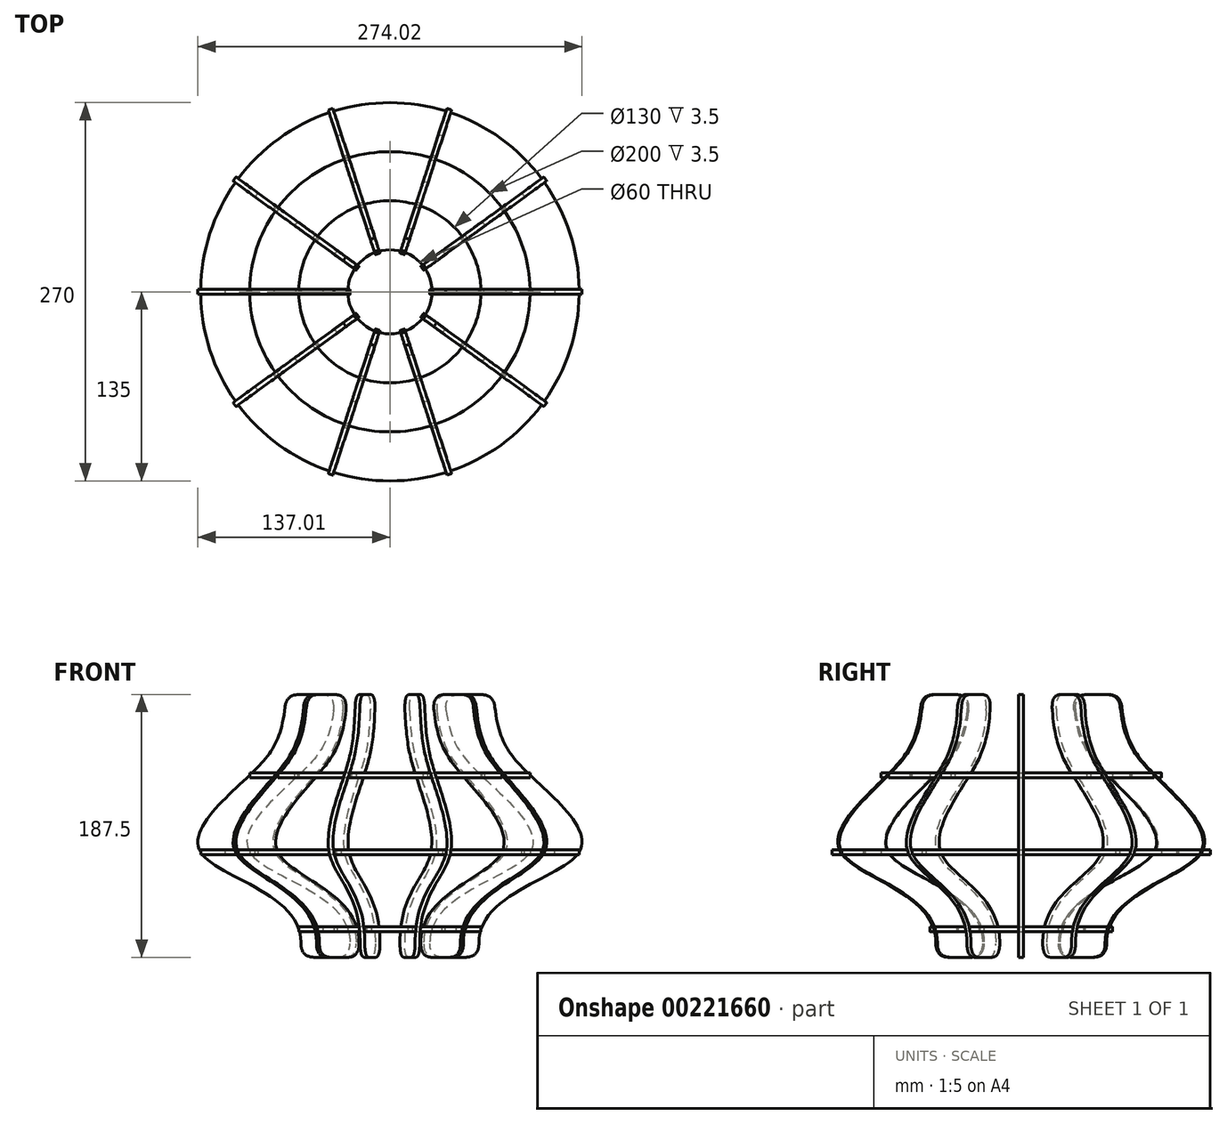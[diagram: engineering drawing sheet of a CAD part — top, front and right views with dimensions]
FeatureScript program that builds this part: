
annotation { "Feature Type Name" : "Feature", "Feature Type Description" : "" }
export const myFeature = defineFeature(function(context is Context, id is Id, definition is map)
    precondition{}
    {
        {
            assignVariable(context, id + "F0", {"name" : "m_thick", "anyValue" : 3.5 * mm});
        }
        {
            var Q0;
            Q0=qCreatedBy(makeId("Front.planeOp"),FACE);
            var sketch = newSketch(context, id + "F1", { "sketchPlane" : qUnion([Q0])});
            skFitSpline(sketch, "E0", {"points": [v(-74.04, 187.5) * mm, v(-100, 130) * mm, v(-135, 75) * mm, v(-65, 0) * mm], "startDerivative": vector(-20.16, -307.27) * mm, "endDerivative": vector(-98.43, -348.48) * mm});
            skLineSegment(sketch, "E1", {"start": v(-74.04, 187.5) * mm, "end": v(-39.04, 187.5) * mm});
            skLineSegment(sketch, "E2", {"start": v(-100, 130) * mm, "end": v(-65, 130) * mm, "construction": true});
            skLineSegment(sketch, "E3", {"start": v(-135, 75) * mm, "end": v(-100, 75) * mm, "construction": true});
            skLineSegment(sketch, "E4", {"start": v(-65, 0) * mm, "end": v(-30, 0) * mm});
            skLineSegment(sketch, "E5", {"start": v(-76.08, 156.38) * mm, "end": v(-41.08, 156.38) * mm, "construction": true});
            skLineSegment(sketch, "E6", {"start": v(-52.3, 45) * mm, "end": v(-17.3, 45) * mm, "construction": true});
            skFitSpline(sketch, "E7", {"points": [v(-39.04, 187.5) * mm, v(-65, 130) * mm, v(-100, 75) * mm, v(-30, 0) * mm], "startDerivative": vector(-20.16, -307.27) * mm, "endDerivative": vector(-98.43, -348.48) * mm});
            skLineSegment(sketch, "E8", {"start": v(-65, 0) * mm, "end": v(-65, 130) * mm, "construction": true});
            skLineSegment(sketch, "E9", {"start": v(-100, 130) * mm, "end": v(-100, 75) * mm, "construction": true});
            skLineSegment(sketch, "E10.bottom", {"start": v(-63.18, 131.75) * mm, "end": v(-100, 131.75) * mm});
            skLineSegment(sketch, "E10.top", {"start": v(-65, 128.25) * mm, "end": v(-100, 128.25) * mm});
            skLineSegment(sketch, "E10.left", {"start": v(-65, 131.75) * mm, "end": v(-65, 128.25) * mm});
            skLineSegment(sketch, "E10.right", {"start": v(-100, 131.75) * mm, "end": v(-100, 128.25) * mm});
            skPoint(sketch, "E10.middle", {"position": v(-82.5, 130) * mm});
            skLineSegment(sketch, "E11", {"start": v(-82.5, 128.25) * mm, "end": v(-82.5, 131.75) * mm});
            skLineSegment(sketch, "E12", {"start": v(-30, 20) * mm, "end": v(-65, 20) * mm, "construction": true});
            skLineSegment(sketch, "E13.bottom", {"start": v(-100, 76.75) * mm, "end": v(-135, 76.75) * mm});
            skLineSegment(sketch, "E13.top", {"start": v(-98.78, 73.25) * mm, "end": v(-135, 73.25) * mm});
            skLineSegment(sketch, "E13.left", {"start": v(-100, 76.75) * mm, "end": v(-100, 73.25) * mm});
            skLineSegment(sketch, "E13.right", {"start": v(-135, 76.75) * mm, "end": v(-135, 73.25) * mm});
            skPoint(sketch, "E13.middle", {"position": v(-117.5, 75) * mm});
            skLineSegment(sketch, "E14.bottom", {"start": v(-30, 21.75) * mm, "end": v(-65, 21.75) * mm});
            skLineSegment(sketch, "E14.top", {"start": v(-29.48, 18.25) * mm, "end": v(-65, 18.25) * mm});
            skLineSegment(sketch, "E14.left", {"start": v(-30, 21.75) * mm, "end": v(-30, 18.25) * mm});
            skLineSegment(sketch, "E14.right", {"start": v(-65, 21.75) * mm, "end": v(-65, 18.25) * mm});
            skPoint(sketch, "E14.middle", {"position": v(-47.5, 20) * mm});
            skLineSegment(sketch, "E15", {"start": v(-47.5, 18.25) * mm, "end": v(-47.5, 21.75) * mm});
            skLineSegment(sketch, "E16", {"start": v(-117.5, 73.25) * mm, "end": v(-117.5, 76.75) * mm});
            skLineSegment(sketch, "E17", {"start": v(0, 0) * mm, "end": v(0, 138.87) * mm, "construction": true});
            skSolve(sketch);
        }
        {
            var Q0;
            {var subQ1=sQuery(id+"F1.wireOp",EDGE,"E1");Q0=makeQuery(id+"F1.imprint","IMPRINT",FACE,{"disambiguationData":[TD([[makeQuery(id+"F1.imprint","IMPRINT",EDGE,{"derivedFrom":subQ1}),-1.0]])]});}
            var Q1;
            {var subQ0=sQuery(id+"F1.wireOp",EDGE,"E10.right");var subQ8=sQuery(id+"F1.wireOp",EDGE,"E0");var subQ9=makeQuery(id+"F1.imprint","INTERSECT",VERTEX,{"derivedFrom":[subQ8,subQ0]});Q1=makeQuery(id+"F1.imprint","IMPRINT",FACE,{"disambiguationData":[TD([[makeQuery(id+"F1.imprint","IMPRINT",EDGE,{"disambiguationData":[TD([[subQ9,-1.0]])],"derivedFrom":subQ8}),1.0]])]});}
            var Q2;
            {var subQ0=sQuery(id+"F1.wireOp",EDGE,"E13.top");var subQ7=sQuery(id+"F1.wireOp",EDGE,"E0");var subQ8=makeQuery(id+"F1.imprint","INTERSECT",VERTEX,{"derivedFrom":[subQ7,subQ0]});Q2=makeQuery(id+"F1.imprint","IMPRINT",FACE,{"disambiguationData":[TD([[makeQuery(id+"F1.imprint","IMPRINT",EDGE,{"disambiguationData":[TD([[subQ8,-1.0]])],"derivedFrom":subQ7}),1.0]])]});}
            var Q3;
            {var subQ7=sQuery(id+"F1.wireOp",EDGE,"E16");Q3=makeQuery(id+"F1.imprint","IMPRINT",FACE,{"disambiguationData":[TD([[makeQuery(id+"F1.imprint","IMPRINT",EDGE,{"derivedFrom":subQ7}),1.0]])]});}
            var Q4;
            {var subQ5=sQuery(id+"F1.wireOp",EDGE,"E11");Q4=makeQuery(id+"F1.imprint","IMPRINT",FACE,{"disambiguationData":[TD([[makeQuery(id+"F1.imprint","IMPRINT",EDGE,{"derivedFrom":subQ5}),1.0]])]});}
            var Q5;
            {var subQ3=sQuery(id+"F1.wireOp",EDGE,"E15");Q5=makeQuery(id+"F1.imprint","IMPRINT",FACE,{"disambiguationData":[TD([[makeQuery(id+"F1.imprint","IMPRINT",EDGE,{"derivedFrom":subQ3}),1.0]])]});}
            var Q6;
            {var subQ8=sQuery(id+"F1.wireOp",EDGE,"E4");Q6=makeQuery(id+"F1.imprint","IMPRINT",FACE,{"disambiguationData":[TD([[makeQuery(id+"F1.imprint","IMPRINT",EDGE,{"derivedFrom":subQ8}),1.0]])]});}
            extrude(context, id + "F2", {"entities" : qUnion([Q0, Q1, Q2, Q3, Q4, Q5, Q6]), "endBound" : BoundingType.SYMMETRIC, "depth" : getVariable(context, 'm_thick')});
        }
        {
            var Q0;
            {var subQ0=sQuery(id+"F1.wireOp",EDGE,"E10.bottom");var subQ1=sQuery(id+"F1.wireOp",EDGE,"E0");var subQ2=makeQuery(id+"F1.imprint","INTERSECT",VERTEX,{"derivedFrom":[subQ1,subQ0]});Q0=makeQuery(id+"F1.imprint","IMPRINT",FACE,{"disambiguationData":[TD([[makeQuery(id+"F1.imprint","IMPRINT",EDGE,{"disambiguationData":[TD([[subQ2,-1.0]])],"derivedFrom":subQ1}),-1.0]])]});}
            var Q1;
            {var subQ5=sQuery(id+"F1.wireOp",EDGE,"E11");Q1=makeQuery(id+"F1.imprint","IMPRINT",FACE,{"disambiguationData":[TD([[makeQuery(id+"F1.imprint","IMPRINT",EDGE,{"derivedFrom":subQ5}),1.0]])]});}
            var Q2;
            {var subQ5=sQuery(id+"F1.wireOp",EDGE,"E11");Q2=makeQuery(id+"F1.imprint","IMPRINT",FACE,{"disambiguationData":[TD([[makeQuery(id+"F1.imprint","IMPRINT",EDGE,{"derivedFrom":subQ5}),-1.0]])]});}
            var Q3;
            {var subQ0=sQuery(id+"F1.wireOp",EDGE,"E10.left");var subQ1=sQuery(id+"F1.wireOp",EDGE,"E7");var subQ2=makeQuery(id+"F1.imprint","INTERSECT",VERTEX,{"derivedFrom":[subQ1,subQ0]});Q3=makeQuery(id+"F1.imprint","IMPRINT",FACE,{"disambiguationData":[TD([[makeQuery(id+"F1.imprint","IMPRINT",EDGE,{"disambiguationData":[TD([[subQ2,-1.0]])],"derivedFrom":subQ1}),1.0]])]});}
            var Q4;
            {var subQ0=sQuery(id+"F1.wireOp",EDGE,"E13.right");var subQ1=sQuery(id+"F1.wireOp",EDGE,"E0");var subQ2=makeQuery(id+"F1.imprint","INTERSECT",VERTEX,{"derivedFrom":[subQ1,subQ0]});Q4=makeQuery(id+"F1.imprint","IMPRINT",FACE,{"disambiguationData":[TD([[makeQuery(id+"F1.imprint","IMPRINT",EDGE,{"disambiguationData":[TD([[subQ2,-1.0]])],"derivedFrom":subQ1}),-1.0]])]});}
            var Q5;
            {var subQ7=sQuery(id+"F1.wireOp",EDGE,"E16");Q5=makeQuery(id+"F1.imprint","IMPRINT",FACE,{"disambiguationData":[TD([[makeQuery(id+"F1.imprint","IMPRINT",EDGE,{"derivedFrom":subQ7}),1.0]])]});}
            var Q6;
            {var subQ0=sQuery(id+"F1.wireOp",EDGE,"E13.bottom");var subQ1=sQuery(id+"F1.wireOp",EDGE,"E7");var subQ2=makeQuery(id+"F1.imprint","INTERSECT",VERTEX,{"derivedFrom":[subQ1,subQ0]});Q6=makeQuery(id+"F1.imprint","IMPRINT",FACE,{"disambiguationData":[TD([[makeQuery(id+"F1.imprint","IMPRINT",EDGE,{"disambiguationData":[TD([[subQ2,-1.0]])],"derivedFrom":subQ1}),1.0]])]});}
            var Q7;
            {var subQ5=sQuery(id+"F1.wireOp",EDGE,"E16");Q7=makeQuery(id+"F1.imprint","IMPRINT",FACE,{"disambiguationData":[TD([[makeQuery(id+"F1.imprint","IMPRINT",EDGE,{"derivedFrom":subQ5}),-1.0]])]});}
            var Q8;
            {var subQ0=sQuery(id+"F1.wireOp",EDGE,"E14.left");var subQ1=sQuery(id+"F1.wireOp",EDGE,"E7");var subQ2=makeQuery(id+"F1.imprint","INTERSECT",VERTEX,{"disambiguationData":[OD(1.0)],"derivedFrom":[subQ1,subQ0]});Q8=makeQuery(id+"F1.imprint","IMPRINT",FACE,{"disambiguationData":[TD([[makeQuery(id+"F1.imprint","IMPRINT",EDGE,{"disambiguationData":[TD([[subQ2,-1.0]])],"derivedFrom":subQ1}),1.0]])]});}
            var Q9;
            {var subQ0=sQuery(id+"F1.wireOp",EDGE,"E14.bottom");var subQ1=sQuery(id+"F1.wireOp",EDGE,"E7");var subQ2=makeQuery(id+"F1.imprint","INTERSECT",VERTEX,{"derivedFrom":[subQ1,subQ0]});Q9=makeQuery(id+"F1.imprint","IMPRINT",FACE,{"disambiguationData":[TD([[makeQuery(id+"F1.imprint","IMPRINT",EDGE,{"disambiguationData":[TD([[subQ2,-1.0]])],"derivedFrom":subQ1}),1.0]])]});}
            var Q10;
            {var subQ0=sQuery(id+"F1.wireOp",EDGE,"E15");Q10=makeQuery(id+"F1.imprint","IMPRINT",FACE,{"disambiguationData":[TD([[makeQuery(id+"F1.imprint","IMPRINT",EDGE,{"derivedFrom":subQ0}),-1.0]])]});}
            var Q11;
            {var subQ3=sQuery(id+"F1.wireOp",EDGE,"E15");Q11=makeQuery(id+"F1.imprint","IMPRINT",FACE,{"disambiguationData":[TD([[makeQuery(id+"F1.imprint","IMPRINT",EDGE,{"derivedFrom":subQ3}),1.0]])]});}
            var Q12;
            {var subQ0=sQuery(id+"F1.wireOp",EDGE,"E14.right");var subQ1=sQuery(id+"F1.wireOp",EDGE,"E0");var subQ2=makeQuery(id+"F1.imprint","INTERSECT",VERTEX,{"derivedFrom":[subQ1,subQ0]});Q12=makeQuery(id+"F1.imprint","IMPRINT",FACE,{"disambiguationData":[TD([[makeQuery(id+"F1.imprint","IMPRINT",EDGE,{"disambiguationData":[TD([[subQ2,-1.0]])],"derivedFrom":subQ1}),-1.0]])]});}
            var Q13;
            Q13=sQuery(id+"F1.wireOp",EDGE,"E17");
            revolve(context, id + "F3", {"entities" : qUnion([Q0, Q1, Q2, Q3, Q4, Q5, Q6, Q7, Q8, Q9, Q10, Q11, Q12]), "axis" : qUnion([Q13]), "revolveType" : RevolveType.FULL});
        }
        {
            var Q0;
            Q0=makeQuery(id+"F2.opExtrude","SWEPT_EDGE",EDGE,{"disambiguationData":[OSD([sQuery(id+"F1.wireOp",EDGE,"E0"),sQuery(id+"F1.wireOp",EDGE,"E4")])]});
            var Q1;
            Q1=makeQuery(id+"F2.opExtrude","SWEPT_EDGE",EDGE,{"disambiguationData":[OSD([sQuery(id+"F1.wireOp",EDGE,"E4"),sQuery(id+"F1.wireOp",EDGE,"E7")])]});
            var Q2;
            Q2=makeQuery(id+"F2.opExtrude","SWEPT_EDGE",EDGE,{"disambiguationData":[OSD([sQuery(id+"F1.wireOp",EDGE,"E0"),sQuery(id+"F1.wireOp",EDGE,"E1")])]});
            var Q3;
            Q3=makeQuery(id+"F2.opExtrude","SWEPT_EDGE",EDGE,{"disambiguationData":[OSD([sQuery(id+"F1.wireOp",EDGE,"E1"),sQuery(id+"F1.wireOp",EDGE,"E7")])]});
            fillet(context, id + "F4", {"entities" : qUnion([Q0, Q1, Q2, Q3]), "radius" : 10 * mm, "tangentPropagation" : true, "rho" : .5, "crossSection" : FilletCrossSection.CONIC, "allowEdgeOverflow" : false});
        }
        {
            var Q0;
            Q0=makeQuery(id+"F2.opExtrude","SWEPT_BODY",BODY,{"disambiguationData":[OSD([sQuery(id+"F1.wireOp",EDGE,"E0"),sQuery(id+"F1.wireOp",EDGE,"E1"),sQuery(id+"F1.wireOp",EDGE,"E4"),sQuery(id+"F1.wireOp",EDGE,"E7"),sQuery(id+"F1.wireOp",EDGE,"E10.bottom"),sQuery(id+"F1.wireOp",EDGE,"E10.top"),sQuery(id+"F1.wireOp",EDGE,"E11"),sQuery(id+"F1.wireOp",EDGE,"E13.bottom"),sQuery(id+"F1.wireOp",EDGE,"E13.top"),sQuery(id+"F1.wireOp",EDGE,"E14.bottom"),sQuery(id+"F1.wireOp",EDGE,"E14.top"),sQuery(id+"F1.wireOp",EDGE,"E14.left"),sQuery(id+"F1.wireOp",EDGE,"E15"),sQuery(id+"F1.wireOp",EDGE,"E16")])]});
            var Q1;
            Q1=makeQuery(id+"F3.opRevolve","SWEPT_EDGE",EDGE,{"disambiguationData":[OSD([sQuery(id+"F1.wireOp",EDGE,"E14.top"),sQuery(id+"F1.wireOp",EDGE,"E14.right")])]});
            circularPattern(context, id + "F5", {"entities" : qUnion([Q0]), "axis" : qUnion([Q1]), "angle" : 360 * degree, "instanceCount" : 10, "equalSpace" : true});
        }
        {
            var Q0;
            Q0=makeQuery(id+"F2.opExtrude","SWEPT_BODY",BODY,{"disambiguationData":[OSD([sQuery(id+"F1.wireOp",EDGE,"E0"),sQuery(id+"F1.wireOp",EDGE,"E1"),sQuery(id+"F1.wireOp",EDGE,"E4"),sQuery(id+"F1.wireOp",EDGE,"E7"),sQuery(id+"F1.wireOp",EDGE,"E10.bottom"),sQuery(id+"F1.wireOp",EDGE,"E10.top"),sQuery(id+"F1.wireOp",EDGE,"E11"),sQuery(id+"F1.wireOp",EDGE,"E13.bottom"),sQuery(id+"F1.wireOp",EDGE,"E13.top"),sQuery(id+"F1.wireOp",EDGE,"E14.bottom"),sQuery(id+"F1.wireOp",EDGE,"E14.top"),sQuery(id+"F1.wireOp",EDGE,"E14.left"),sQuery(id+"F1.wireOp",EDGE,"E15"),sQuery(id+"F1.wireOp",EDGE,"E16")])]});
            var Q1;
            Q1=makeQuery(id+"F5.opPattern","COPY",BODY,{"derivedFrom":makeQuery(id+"F2.opExtrude","SWEPT_BODY",BODY,{"disambiguationData":[OSD([sQuery(id+"F1.wireOp",EDGE,"E0"),sQuery(id+"F1.wireOp",EDGE,"E1"),sQuery(id+"F1.wireOp",EDGE,"E4"),sQuery(id+"F1.wireOp",EDGE,"E7"),sQuery(id+"F1.wireOp",EDGE,"E10.bottom"),sQuery(id+"F1.wireOp",EDGE,"E10.top"),sQuery(id+"F1.wireOp",EDGE,"E11"),sQuery(id+"F1.wireOp",EDGE,"E13.bottom"),sQuery(id+"F1.wireOp",EDGE,"E13.top"),sQuery(id+"F1.wireOp",EDGE,"E14.bottom"),sQuery(id+"F1.wireOp",EDGE,"E14.top"),sQuery(id+"F1.wireOp",EDGE,"E14.left"),sQuery(id+"F1.wireOp",EDGE,"E15"),sQuery(id+"F1.wireOp",EDGE,"E16")])]}),"instanceName":"1"});
            var Q2;
            Q2=makeQuery(id+"F5.opPattern","COPY",BODY,{"derivedFrom":makeQuery(id+"F2.opExtrude","SWEPT_BODY",BODY,{"disambiguationData":[OSD([sQuery(id+"F1.wireOp",EDGE,"E0"),sQuery(id+"F1.wireOp",EDGE,"E1"),sQuery(id+"F1.wireOp",EDGE,"E4"),sQuery(id+"F1.wireOp",EDGE,"E7"),sQuery(id+"F1.wireOp",EDGE,"E10.bottom"),sQuery(id+"F1.wireOp",EDGE,"E10.top"),sQuery(id+"F1.wireOp",EDGE,"E11"),sQuery(id+"F1.wireOp",EDGE,"E13.bottom"),sQuery(id+"F1.wireOp",EDGE,"E13.top"),sQuery(id+"F1.wireOp",EDGE,"E14.bottom"),sQuery(id+"F1.wireOp",EDGE,"E14.top"),sQuery(id+"F1.wireOp",EDGE,"E14.left"),sQuery(id+"F1.wireOp",EDGE,"E15"),sQuery(id+"F1.wireOp",EDGE,"E16")])]}),"instanceName":"2"});
            var Q3;
            Q3=makeQuery(id+"F5.opPattern","COPY",BODY,{"derivedFrom":makeQuery(id+"F2.opExtrude","SWEPT_BODY",BODY,{"disambiguationData":[OSD([sQuery(id+"F1.wireOp",EDGE,"E0"),sQuery(id+"F1.wireOp",EDGE,"E1"),sQuery(id+"F1.wireOp",EDGE,"E4"),sQuery(id+"F1.wireOp",EDGE,"E7"),sQuery(id+"F1.wireOp",EDGE,"E10.bottom"),sQuery(id+"F1.wireOp",EDGE,"E10.top"),sQuery(id+"F1.wireOp",EDGE,"E11"),sQuery(id+"F1.wireOp",EDGE,"E13.bottom"),sQuery(id+"F1.wireOp",EDGE,"E13.top"),sQuery(id+"F1.wireOp",EDGE,"E14.bottom"),sQuery(id+"F1.wireOp",EDGE,"E14.top"),sQuery(id+"F1.wireOp",EDGE,"E14.left"),sQuery(id+"F1.wireOp",EDGE,"E15"),sQuery(id+"F1.wireOp",EDGE,"E16")])]}),"instanceName":"3"});
            var Q4;
            Q4=makeQuery(id+"F5.opPattern","COPY",BODY,{"derivedFrom":makeQuery(id+"F2.opExtrude","SWEPT_BODY",BODY,{"disambiguationData":[OSD([sQuery(id+"F1.wireOp",EDGE,"E0"),sQuery(id+"F1.wireOp",EDGE,"E1"),sQuery(id+"F1.wireOp",EDGE,"E4"),sQuery(id+"F1.wireOp",EDGE,"E7"),sQuery(id+"F1.wireOp",EDGE,"E10.bottom"),sQuery(id+"F1.wireOp",EDGE,"E10.top"),sQuery(id+"F1.wireOp",EDGE,"E11"),sQuery(id+"F1.wireOp",EDGE,"E13.bottom"),sQuery(id+"F1.wireOp",EDGE,"E13.top"),sQuery(id+"F1.wireOp",EDGE,"E14.bottom"),sQuery(id+"F1.wireOp",EDGE,"E14.top"),sQuery(id+"F1.wireOp",EDGE,"E14.left"),sQuery(id+"F1.wireOp",EDGE,"E15"),sQuery(id+"F1.wireOp",EDGE,"E16")])]}),"instanceName":"4"});
            var Q5;
            Q5=makeQuery(id+"F5.opPattern","COPY",BODY,{"derivedFrom":makeQuery(id+"F2.opExtrude","SWEPT_BODY",BODY,{"disambiguationData":[OSD([sQuery(id+"F1.wireOp",EDGE,"E0"),sQuery(id+"F1.wireOp",EDGE,"E1"),sQuery(id+"F1.wireOp",EDGE,"E4"),sQuery(id+"F1.wireOp",EDGE,"E7"),sQuery(id+"F1.wireOp",EDGE,"E10.bottom"),sQuery(id+"F1.wireOp",EDGE,"E10.top"),sQuery(id+"F1.wireOp",EDGE,"E11"),sQuery(id+"F1.wireOp",EDGE,"E13.bottom"),sQuery(id+"F1.wireOp",EDGE,"E13.top"),sQuery(id+"F1.wireOp",EDGE,"E14.bottom"),sQuery(id+"F1.wireOp",EDGE,"E14.top"),sQuery(id+"F1.wireOp",EDGE,"E14.left"),sQuery(id+"F1.wireOp",EDGE,"E15"),sQuery(id+"F1.wireOp",EDGE,"E16")])]}),"instanceName":"5"});
            var Q6;
            Q6=makeQuery(id+"F5.opPattern","COPY",BODY,{"derivedFrom":makeQuery(id+"F2.opExtrude","SWEPT_BODY",BODY,{"disambiguationData":[OSD([sQuery(id+"F1.wireOp",EDGE,"E0"),sQuery(id+"F1.wireOp",EDGE,"E1"),sQuery(id+"F1.wireOp",EDGE,"E4"),sQuery(id+"F1.wireOp",EDGE,"E7"),sQuery(id+"F1.wireOp",EDGE,"E10.bottom"),sQuery(id+"F1.wireOp",EDGE,"E10.top"),sQuery(id+"F1.wireOp",EDGE,"E11"),sQuery(id+"F1.wireOp",EDGE,"E13.bottom"),sQuery(id+"F1.wireOp",EDGE,"E13.top"),sQuery(id+"F1.wireOp",EDGE,"E14.bottom"),sQuery(id+"F1.wireOp",EDGE,"E14.top"),sQuery(id+"F1.wireOp",EDGE,"E14.left"),sQuery(id+"F1.wireOp",EDGE,"E15"),sQuery(id+"F1.wireOp",EDGE,"E16")])]}),"instanceName":"6"});
            var Q7;
            Q7=makeQuery(id+"F5.opPattern","COPY",BODY,{"derivedFrom":makeQuery(id+"F2.opExtrude","SWEPT_BODY",BODY,{"disambiguationData":[OSD([sQuery(id+"F1.wireOp",EDGE,"E0"),sQuery(id+"F1.wireOp",EDGE,"E1"),sQuery(id+"F1.wireOp",EDGE,"E4"),sQuery(id+"F1.wireOp",EDGE,"E7"),sQuery(id+"F1.wireOp",EDGE,"E10.bottom"),sQuery(id+"F1.wireOp",EDGE,"E10.top"),sQuery(id+"F1.wireOp",EDGE,"E11"),sQuery(id+"F1.wireOp",EDGE,"E13.bottom"),sQuery(id+"F1.wireOp",EDGE,"E13.top"),sQuery(id+"F1.wireOp",EDGE,"E14.bottom"),sQuery(id+"F1.wireOp",EDGE,"E14.top"),sQuery(id+"F1.wireOp",EDGE,"E14.left"),sQuery(id+"F1.wireOp",EDGE,"E15"),sQuery(id+"F1.wireOp",EDGE,"E16")])]}),"instanceName":"7"});
            var Q8;
            Q8=makeQuery(id+"F5.opPattern","COPY",BODY,{"derivedFrom":makeQuery(id+"F2.opExtrude","SWEPT_BODY",BODY,{"disambiguationData":[OSD([sQuery(id+"F1.wireOp",EDGE,"E0"),sQuery(id+"F1.wireOp",EDGE,"E1"),sQuery(id+"F1.wireOp",EDGE,"E4"),sQuery(id+"F1.wireOp",EDGE,"E7"),sQuery(id+"F1.wireOp",EDGE,"E10.bottom"),sQuery(id+"F1.wireOp",EDGE,"E10.top"),sQuery(id+"F1.wireOp",EDGE,"E11"),sQuery(id+"F1.wireOp",EDGE,"E13.bottom"),sQuery(id+"F1.wireOp",EDGE,"E13.top"),sQuery(id+"F1.wireOp",EDGE,"E14.bottom"),sQuery(id+"F1.wireOp",EDGE,"E14.top"),sQuery(id+"F1.wireOp",EDGE,"E14.left"),sQuery(id+"F1.wireOp",EDGE,"E15"),sQuery(id+"F1.wireOp",EDGE,"E16")])]}),"instanceName":"8"});
            var Q9;
            Q9=makeQuery(id+"F5.opPattern","COPY",BODY,{"derivedFrom":makeQuery(id+"F2.opExtrude","SWEPT_BODY",BODY,{"disambiguationData":[OSD([sQuery(id+"F1.wireOp",EDGE,"E0"),sQuery(id+"F1.wireOp",EDGE,"E1"),sQuery(id+"F1.wireOp",EDGE,"E4"),sQuery(id+"F1.wireOp",EDGE,"E7"),sQuery(id+"F1.wireOp",EDGE,"E10.bottom"),sQuery(id+"F1.wireOp",EDGE,"E10.top"),sQuery(id+"F1.wireOp",EDGE,"E11"),sQuery(id+"F1.wireOp",EDGE,"E13.bottom"),sQuery(id+"F1.wireOp",EDGE,"E13.top"),sQuery(id+"F1.wireOp",EDGE,"E14.bottom"),sQuery(id+"F1.wireOp",EDGE,"E14.top"),sQuery(id+"F1.wireOp",EDGE,"E14.left"),sQuery(id+"F1.wireOp",EDGE,"E15"),sQuery(id+"F1.wireOp",EDGE,"E16")])]}),"instanceName":"9"});
            var Q10;
            Q10=makeQuery(id+"F3.opRevolve","SWEPT_BODY",BODY,{"disambiguationData":[OSD([sQuery(id+"F1.wireOp",EDGE,"E14.bottom"),sQuery(id+"F1.wireOp",EDGE,"E14.top"),sQuery(id+"F1.wireOp",EDGE,"E14.left"),sQuery(id+"F1.wireOp",EDGE,"E14.right")])]});
            var Q11;
            Q11=makeQuery(id+"F3.opRevolve","SWEPT_BODY",BODY,{"disambiguationData":[OSD([sQuery(id+"F1.wireOp",EDGE,"E13.bottom"),sQuery(id+"F1.wireOp",EDGE,"E13.top"),sQuery(id+"F1.wireOp",EDGE,"E13.left"),sQuery(id+"F1.wireOp",EDGE,"E13.right")])]});
            var Q12;
            Q12=makeQuery(id+"F3.opRevolve","SWEPT_BODY",BODY,{"disambiguationData":[OSD([sQuery(id+"F1.wireOp",EDGE,"E10.bottom"),sQuery(id+"F1.wireOp",EDGE,"E10.top"),sQuery(id+"F1.wireOp",EDGE,"E10.left"),sQuery(id+"F1.wireOp",EDGE,"E10.right")])]});
            var Q13;
            Q13=makeQuery(id+"F2.opExtrude","SWEPT_FACE",FACE,{"disambiguationData":[OSD([sQuery(id+"F1.wireOp",EDGE,"E0")])]});
            var Q14;
            Q14=makeQuery(id+"F5.opPattern","COPY",FACE,{"derivedFrom":makeQuery(id+"F2.opExtrude","SWEPT_FACE",FACE,{"disambiguationData":[OSD([sQuery(id+"F1.wireOp",EDGE,"E0")])]}),"instanceName":"9"});
            var Q15;
            Q15=makeQuery(id+"F5.opPattern","COPY",FACE,{"derivedFrom":makeQuery(id+"F2.opExtrude","SWEPT_FACE",FACE,{"disambiguationData":[OSD([sQuery(id+"F1.wireOp",EDGE,"E0")])]}),"instanceName":"8"});
            var Q16;
            Q16=makeQuery(id+"F5.opPattern","COPY",FACE,{"derivedFrom":makeQuery(id+"F2.opExtrude","SWEPT_FACE",FACE,{"disambiguationData":[OSD([sQuery(id+"F1.wireOp",EDGE,"E0")])]}),"instanceName":"7"});
            var Q17;
            Q17=makeQuery(id+"F5.opPattern","COPY",FACE,{"derivedFrom":makeQuery(id+"F2.opExtrude","SWEPT_FACE",FACE,{"disambiguationData":[OSD([sQuery(id+"F1.wireOp",EDGE,"E0")])]}),"instanceName":"6"});
            var Q18;
            Q18=makeQuery(id+"F5.opPattern","COPY",FACE,{"derivedFrom":makeQuery(id+"F2.opExtrude","SWEPT_FACE",FACE,{"disambiguationData":[OSD([sQuery(id+"F1.wireOp",EDGE,"E0")])]}),"instanceName":"5"});
            var Q19;
            Q19=makeQuery(id+"F5.opPattern","COPY",FACE,{"derivedFrom":makeQuery(id+"F2.opExtrude","SWEPT_FACE",FACE,{"disambiguationData":[OSD([sQuery(id+"F1.wireOp",EDGE,"E0")])]}),"instanceName":"4"});
            var Q20;
            Q20=makeQuery(id+"F5.opPattern","COPY",FACE,{"derivedFrom":makeQuery(id+"F2.opExtrude","SWEPT_FACE",FACE,{"disambiguationData":[OSD([sQuery(id+"F1.wireOp",EDGE,"E0")])]}),"instanceName":"3"});
            var Q21;
            Q21=makeQuery(id+"F5.opPattern","COPY",FACE,{"derivedFrom":makeQuery(id+"F2.opExtrude","SWEPT_FACE",FACE,{"disambiguationData":[OSD([sQuery(id+"F1.wireOp",EDGE,"E0")])]}),"instanceName":"2"});
            var Q22;
            Q22=makeQuery(id+"F5.opPattern","COPY",FACE,{"derivedFrom":makeQuery(id+"F2.opExtrude","SWEPT_FACE",FACE,{"disambiguationData":[OSD([sQuery(id+"F1.wireOp",EDGE,"E0")])]}),"instanceName":"1"});
            booleanBodies(context, id + "F6", {"operationType" : BooleanOperationType.SUBTRACTION, "tools" : qUnion([Q0, Q1, Q2, Q3, Q4, Q5, Q6, Q7, Q8, Q9]), "targets" : qUnion([Q10, Q11, Q12]), "offset" : true, "entitiesToOffset" : qUnion([Q13, Q14, Q15, Q16, Q17, Q18, Q19, Q20, Q21, Q22]), "offsetDistance" : 2.5 * mm, "keepTools" : true});
        }
    });
